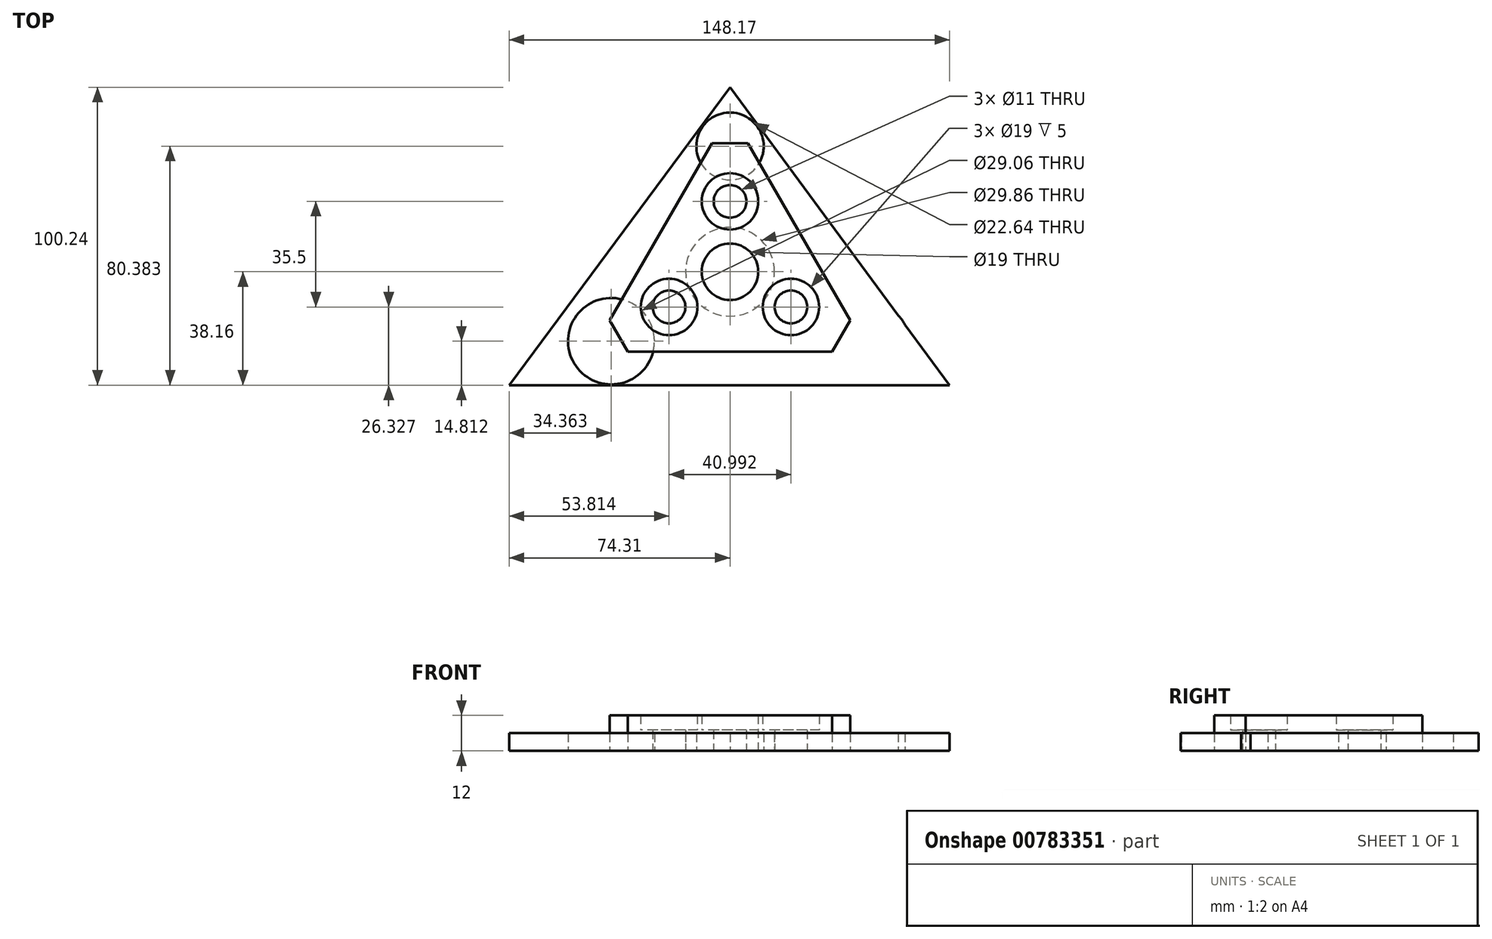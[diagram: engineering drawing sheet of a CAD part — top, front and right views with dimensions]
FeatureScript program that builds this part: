
annotation { "Feature Type Name" : "Feature", "Feature Type Description" : "" }
export const myFeature = defineFeature(function(context is Context, id is Id, definition is map)
    precondition{}
    {
        {
            var Q0;
            Q0=qCreatedBy(makeId("Top.planeOp"),FACE);
            var sketch = newSketch(context, id + "F0", { "sketchPlane" : qUnion([Q0])});
            skLineSegment(sketch, "E0", {"start": v(-49.7, 0) * mm, "end": v(39, 0) * mm});
            skLineSegment(sketch, "E1", {"start": v(0, 62.08) * mm, "end": v(-74.3, -38.16) * mm});
            skLineSegment(sketch, "E2", {"start": v(-74.3, -38.16) * mm, "end": v(73.86, -38.16) * mm});
            skLineSegment(sketch, "E3", {"start": v(73.86, -38.16) * mm, "end": v(0, 62.08) * mm});
            skCircle(sketch, "E4", {"center": v(0, 0) * mm, "radius": 14.93 * mm});
            skCircle(sketch, "E5", {"center": v(0, 42.22) * mm, "radius": 11.32 * mm});
            skCircle(sketch, "E6", {"center": v(-39.95, -23.35) * mm, "radius": 14.53 * mm});
            skCircle(sketch, "E7", {"center": v(46.75, -24.3) * mm, "radius": 13.74 * mm});
            skSolve(sketch);
        }
        {
            var Q0;
            Q0=qCreatedBy(makeId("Top.planeOp"),FACE);
            var sketch = newSketch(context, id + "F1", { "sketchPlane" : qUnion([Q0])});
            skCircle(sketch, "E8.cCircle", {"center": v(0, 0) * mm, "radius": 53.67 * mm, "construction": true});
            skLineSegment(sketch, "E8.0", {"start": v(-46.48, -26.83) * mm, "end": v(0, 53.67) * mm});
            skLineSegment(sketch, "E8.1", {"start": v(0, 53.67) * mm, "end": v(46.48, -26.83) * mm});
            skLineSegment(sketch, "E8.2", {"start": v(46.48, -26.83) * mm, "end": v(-46.48, -26.83) * mm});
            skCircle(sketch, "E9", {"center": v(0, 23.67) * mm, "radius": 5.5 * mm});
            skCircle(sketch, "E10.0", {"center": v(0, 23.67) * mm, "radius": 9.5 * mm});
            skLineSegment(sketch, "E11", {"start": v(-6.06, 43.17) * mm, "end": v(6.06, 43.17) * mm});
            skLineSegment(sketch, "E12.1.0", {"start": v(-34.35, -26.83) * mm, "end": v(-40.41, -16.33) * mm});
            skCircle(sketch, "E12.1.1", {"center": v(-20.5, -11.83) * mm, "radius": 9.5 * mm});
            skCircle(sketch, "E12.1.2", {"center": v(-20.5, -11.83) * mm, "radius": 5.5 * mm});
            skLineSegment(sketch, "E12.2.0", {"start": v(40.41, -16.33) * mm, "end": v(34.35, -26.83) * mm});
            skCircle(sketch, "E12.2.1", {"center": v(20.5, -11.83) * mm, "radius": 9.5 * mm});
            skCircle(sketch, "E12.2.2", {"center": v(20.5, -11.83) * mm, "radius": 5.5 * mm});
            skLineSegment(sketch, "E13", {"start": v(-63.67, 0) * mm, "end": v(-63.67, 23.67) * mm, "construction": true});
            skLineSegment(sketch, "E14", {"start": v(-63.67, 11.83) * mm, "end": v(-83.68, 11.83) * mm, "construction": true});
            skCircle(sketch, "E15.MirrorC", {"center": v(0, 0) * mm, "radius": 9.5 * mm});
            skCircle(sketch, "E16.MirrorC", {"center": v(0, 0) * mm, "radius": 5.5 * mm});
            skSolve(sketch);
        }
        {
            var Q0;
            Q0=makeQuery(id+"F1.imprint","IMPRINT",FACE,{"disambiguationData":[TD([[makeQuery(id+"F1.imprint","IMPRINT",EDGE,{"derivedFrom":sQuery(id+"F1.wireOp",EDGE,"E10.0")}),-1.0]])]});
            var Q1;
            Q1=makeQuery(id+"F1.imprint","IMPRINT",FACE,{"disambiguationData":[TD([[makeQuery(id+"F1.imprint","IMPRINT",EDGE,{"derivedFrom":sQuery(id+"F1.wireOp",EDGE,"E9")}),-1.0]])]});
            var Q2;
            Q2=makeQuery(id+"F1.imprint","IMPRINT",FACE,{"disambiguationData":[TD([[makeQuery(id+"F1.imprint","IMPRINT",EDGE,{"derivedFrom":sQuery(id+"F1.wireOp",EDGE,"E12.1.1")}),1.0]])]});
            var Q3;
            Q3=makeQuery(id+"F1.imprint","IMPRINT",FACE,{"disambiguationData":[TD([[makeQuery(id+"F1.imprint","IMPRINT",EDGE,{"derivedFrom":sQuery(id+"F1.wireOp",EDGE,"E15.MirrorC")}),-1.0]])]});
            var Q4;
            Q4=makeQuery(id+"F1.imprint","IMPRINT",FACE,{"disambiguationData":[TD([[makeQuery(id+"F1.imprint","IMPRINT",EDGE,{"derivedFrom":sQuery(id+"F1.wireOp",EDGE,"E12.2.1")}),1.0]])]});
            extrude(context, id + "F2", {"entities" : qUnion([Q0, Q1, Q2, Q3, Q4]), "depth" : 7 * mm, "offsetDistance" : 25 * mm});
        }
        {
            var Q0;
            Q0=makeQuery(id+"F1.imprint","IMPRINT",FACE,{"disambiguationData":[TD([[makeQuery(id+"F1.imprint","IMPRINT",EDGE,{"derivedFrom":sQuery(id+"F1.wireOp",EDGE,"E10.0")}),-1.0]])]});
            extrude(context, id + "F3", {"entities" : qUnion([Q0]), "operationType" : NewBodyOperationType.ADD, "depth" : 12 * mm, "offsetDistance" : 25 * mm});
        }
        {
            var Q0;
            Q0=qSketchRegion(id+"F0",true);
            extrude(context, id + "F4", {"entities" : qUnion([Q0]), "depth" : 6 * mm, "offsetDistance" : 25 * mm});
        }
        {
            var Q0;
            Q0=sQuery(id+"F0.wireOp",EDGE,"E7");
            extrude(context, id + "F5", {"bodyType" : ToolBodyType.SURFACE, "surfaceEntities" : qUnion([Q0]), "depth" : 6 * mm, "offsetDistance" : 25 * mm});
        }
    });
